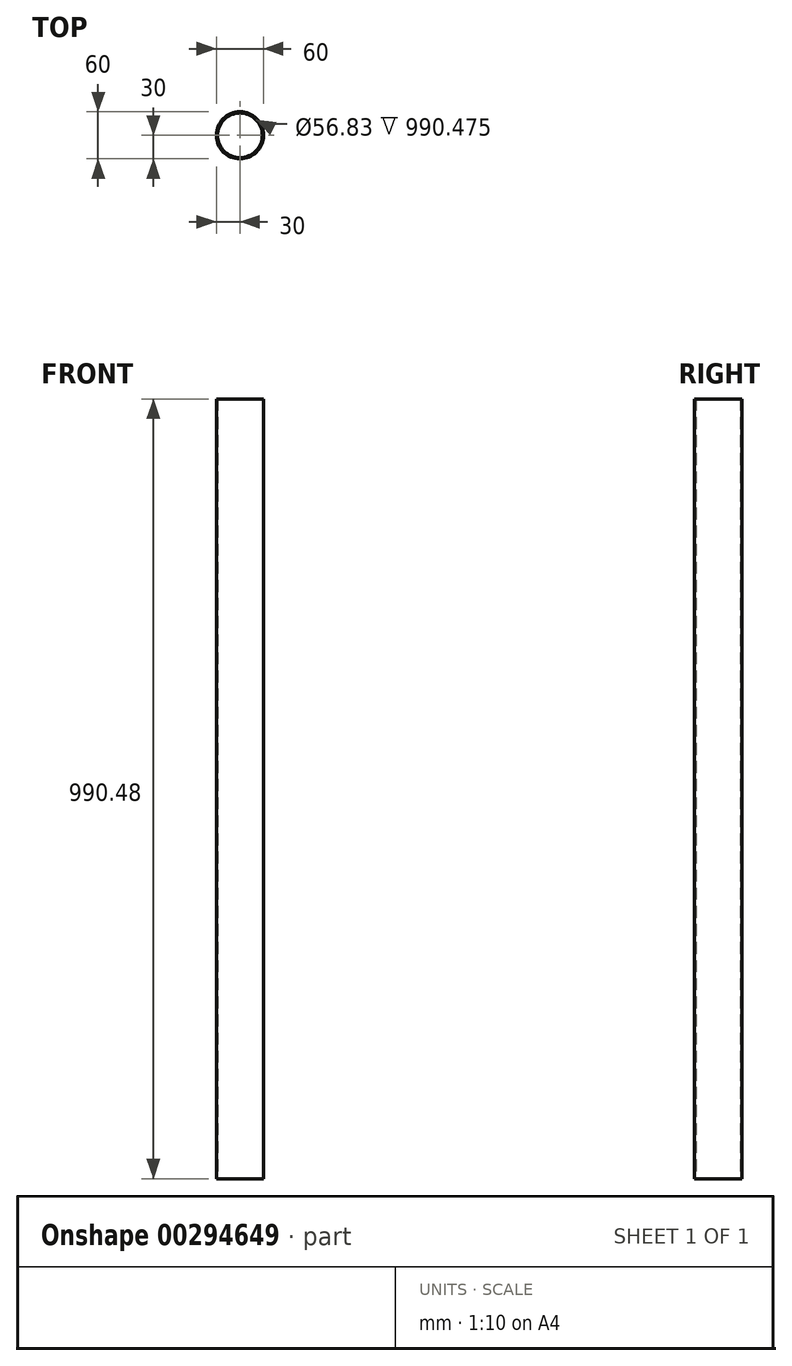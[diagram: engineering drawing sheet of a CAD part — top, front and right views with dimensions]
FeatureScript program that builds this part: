
annotation { "Feature Type Name" : "Feature", "Feature Type Description" : "" }
export const myFeature = defineFeature(function(context is Context, id is Id, definition is map)
    precondition{}
    {
        {
            var Q0;
            Q0=qCreatedBy(makeId("Top.planeOp"),FACE);
            var sketch = newSketch(context, id + "F0", { "sketchPlane" : qUnion([Q0])});
            skCircle(sketch, "E0", {"center": v(0, 0) * mm, "radius": 30 * mm});
            skCircle(sketch, "E1", {"center": v(0, 0) * mm, "radius": 28.41 * mm});
            skSolve(sketch);
        }
        {
            var Q0;
            Q0=makeQuery(id+"F0.imprint","IMPRINT",FACE,{"disambiguationData":[TD([[makeQuery(id+"F0.imprint","IMPRINT",EDGE,{"derivedFrom":sQuery(id+"F0.wireOp",EDGE,"E0")}),1.0]])]});
            extrude(context, id + "F1", {"entities" : qUnion([Q0]), "endBound" : BoundingType.SYMMETRIC, "depth" : 990.48 * mm});
        }
    });
